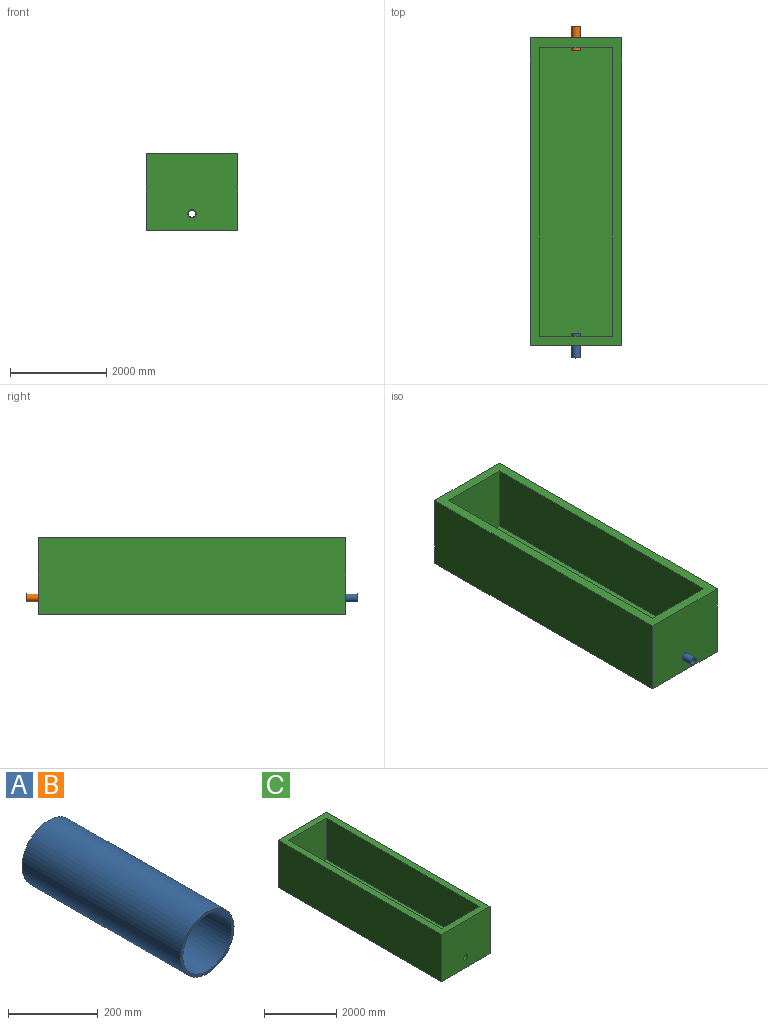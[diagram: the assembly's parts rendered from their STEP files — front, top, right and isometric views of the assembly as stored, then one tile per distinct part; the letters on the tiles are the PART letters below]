
ASSEMBLY  parts=3 mates=1
PART A: 4 faces, bbox 168.3x500x168.3 mm
  f0: cylinder r=77.03mm len=500mm, axis (0,1,0), area 241996.9mm2, adj f2,f3
  f1: cylinder r=84.14mm len=500mm, axis (0,1,0), area 264333.6mm2, adj f2,f3
  f2: plane 168.28x168.28mm, normal (0,-1,0), area 3600mm2, adj f0,f1
  f3: plane 168.28x168.28mm, normal (0,1,0), area 3600mm2, adj f0,f1
PART B: same geometry as A
PART C: 13 faces, bbox 1900x6400x1600 mm
  f0: plane 6400x1900mm, normal (0,0,1), area 3160000mm2, adj f2,f3,f4,f5,f7,f8,f9,f10
  f1: plane 6400x1900mm, normal (0,0,-1), area 12160000mm2, adj f2,f3,f4,f5
  f2: plane 6400x1600mm, normal (1,0,0), area 10240000mm2, adj f0,f1,f4,f5
  f3: plane 6400x1600mm, normal (-1,0,0), area 10240000mm2, adj f0,f1,f4,f5
  f4: plane 1900x1600mm, normal (0,1,0), area 3017759mm2, adj f0,f1,f2,f3,f12
  f5: plane 1900x1600mm, normal (0,-1,0), area 3017759mm2, adj f0,f1,f2,f3,f11
  f6: plane 6000x1500mm, normal (0,0,1), area 9000000mm2, adj f7,f8,f9,f10
  f7: plane 6000x1400mm, normal (-1,0,0), area 8400000mm2, adj f0,f6,f9,f10
  f8: plane 6000x1400mm, normal (1,0,0), area 8400000mm2, adj f0,f6,f9,f10
  f9: plane 1500x1400mm, normal (0,-1,0), area 2077759mm2, adj f0,f6,f7,f8,f12
  f10: plane 1500x1400mm, normal (0,1,0), area 2077759mm2, adj f0,f6,f7,f8,f11
  f11: cylinder r=84.14mm len=200mm, axis (0,-1,0), area 105733.4mm2, adj f5,f10
  f12: cylinder r=84.14mm len=200mm, axis (0,1,0), area 105733.4mm2, adj f4,f9
PLACE A t=(0,0,-452.1)mm
PLACE B t=(0,6400,-450)mm
PLACE C at identity
MATE fastened B.f1 <-> C.f11  axis (0,-1,0) through (0,6400,-450)mm
